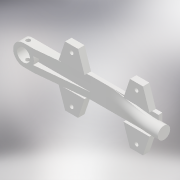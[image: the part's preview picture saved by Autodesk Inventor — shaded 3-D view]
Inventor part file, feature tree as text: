
AUTODESK INVENTOR PART (.ipt)
format: ipt  version: 2018.2 (Build 222227000, 227)  size: 291,840 bytes
history: native  units: mm
features: sketch x8, extrude x7, plane x2, mirror x2, projected_geometry x2, loft x1
ambient origin geometry x8: Origin, YZ Plane, XZ Plane, XY Plane, X Axis, Y Axis, Z Axis, Center Point
bodies: Solid1 (feature_tree)
feature tree (22):
  sketch  "Sketch1"  dims[d0=10.0mm d2=3.0mm]
  extrude  "Extrusion1"  Depth=3.0mm
  extrude  "Extrusion2"  Depth=16.0mm
  plane  "Work Plane1"
  extrude  "Extrusion3"  Depth=3.0mm TaperAngle=0.0deg
  sketch  "Sketch3"  dims[d5=3.0mm d6=0.0mm d7=4.0mm d8=0.0mm]
  plane  "Work Plane2"
  loft  "Loft1"
  extrude  "Extrusion4"  [1 undecoded]
  extrude  "Extrusion5"  Depth=10.0mm TaperAngle=90.0deg
  mirror  "Mirror1"
  extrude  "Extrusion6"  Depth=5.0mm TaperAngle=0.0deg
  extrude  "Extrusion12"  Depth=5.0mm
  mirror  "Mirror4"
  sketch  "Sketch2"  dims[d3=100.0mm d4=16.0mm]
  projected_geometry  "Projected Loop1"
  sketch  "Sketch4"  dims[d9=6.0mm d10=9.525mm]
  sketch  "Sketch6"  dims[d11=6.0mm d12=0.0mm d13=-40.0mm]
  sketch  "Sketch7"  dims[d14=10.0mm d15=90.0deg d16=10.0mm d17=90.0deg]
  projected_geometry  "Projected Loop2"
  sketch  "Sketch8"  dims[d20=40.0mm d21=5.0mm d22=0.0mm]
  sketch  "Sketch14"  dims[d23=5.0mm d24=0.0mm d25=3.2mm d26=5.0mm d27=0.0mm d62=20.0mm d63=10.0mm d64=20.0mm d65=5.0mm d66=5.0mm d67=3.0mm d68=3.0mm d69=45.0mm d70=18.0mm d71=5.0mm d72=35.0mm d73=5.0mm d74=0.0mm]
note: 1 required parameter value undecoded (feature->parameter linkage not recoverable at this tier; creation-order binding heuristic only, values carry confidence <= 0.55)
